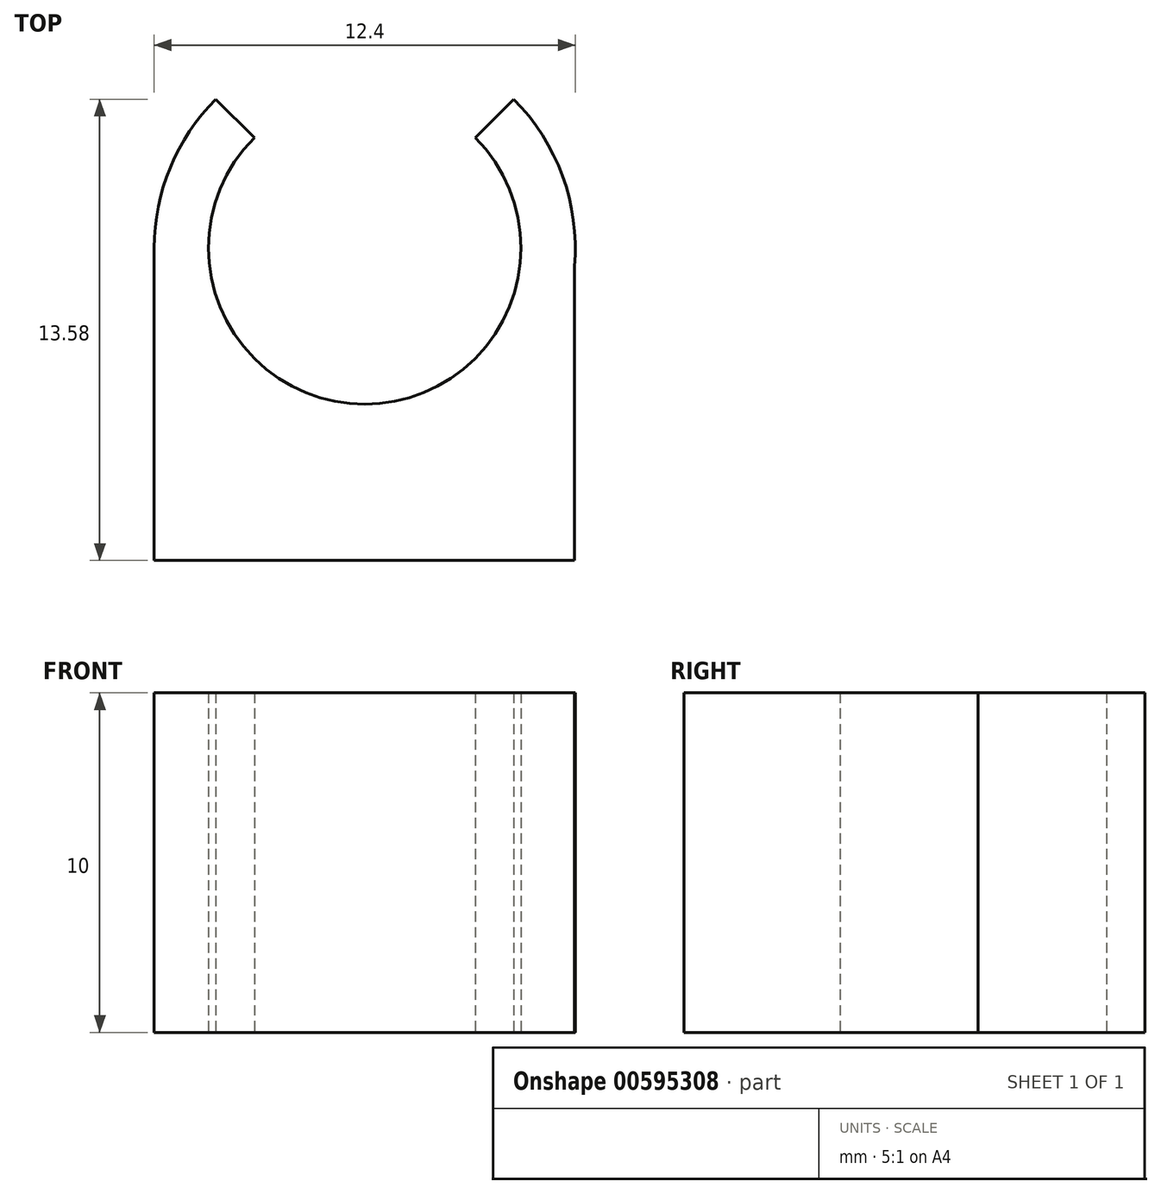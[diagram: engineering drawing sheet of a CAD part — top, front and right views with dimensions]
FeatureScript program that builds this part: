
annotation { "Feature Type Name" : "Feature", "Feature Type Description" : "" }
export const myFeature = defineFeature(function(context is Context, id is Id, definition is map)
    precondition{}
    {
        {
            var Q0;
            Q0=qCreatedBy(makeId("Top.planeOp"),FACE);
            var sketch = newSketch(context, id + "F0", { "sketchPlane" : qUnion([Q0])});
            skCircle(sketch, "E0", {"center": v(0, 0) * mm, "radius": 4.6 * mm});
            skCircle(sketch, "E1", {"center": v(0, 0) * mm, "radius": 6.2 * mm});
            skLineSegment(sketch, "E2", {"start": v(-6.2, 0) * mm, "end": v(-6.2, -9.2) * mm});
            skLineSegment(sketch, "E3", {"start": v(-6.2, -9.2) * mm, "end": v(6.18, -9.2) * mm});
            skLineSegment(sketch, "E4", {"start": v(6.18, -9.2) * mm, "end": v(6.18, -0.53) * mm});
            skLineSegment(sketch, "E5", {"start": v(-4.38, 4.38) * mm, "end": v(0, 0) * mm});
            skLineSegment(sketch, "E6", {"start": v(0, 0) * mm, "end": v(4.38, 4.38) * mm});
            skLineSegment(sketch, "E7", {"start": v(0, 0) * mm, "end": v(0, 6.2) * mm, "construction": true});
            skSolve(sketch);
        }
        {
            var Q0;
            {var subQ0=sQuery(id+"F0.wireOp",EDGE,"E2");Q0=makeQuery(id+"F0.imprint","IMPRINT",FACE,{"disambiguationData":[TD([[makeQuery(id+"F0.imprint","IMPRINT",EDGE,{"derivedFrom":subQ0}),1.0]])]});}
            var Q1;
            {var subQ5=sQuery(id+"F0.wireOp",EDGE,"E5");var subQ7=sQuery(id+"F0.wireOp",EDGE,"E0");var subQ8=makeQuery(id+"F0.imprint","INTERSECT",VERTEX,{"derivedFrom":[subQ7,subQ5]});Q1=makeQuery(id+"F0.imprint","IMPRINT",FACE,{"disambiguationData":[TD([[makeQuery(id+"F0.imprint","IMPRINT",EDGE,{"disambiguationData":[TD([[subQ8,-1.0]])],"derivedFrom":subQ7}),-1.0]])]});}
            extrude(context, id + "F1", {"entities" : qUnion([Q0, Q1]), "depth" : 10 * mm, "offsetDistance" : 25 * mm});
        }
    });
